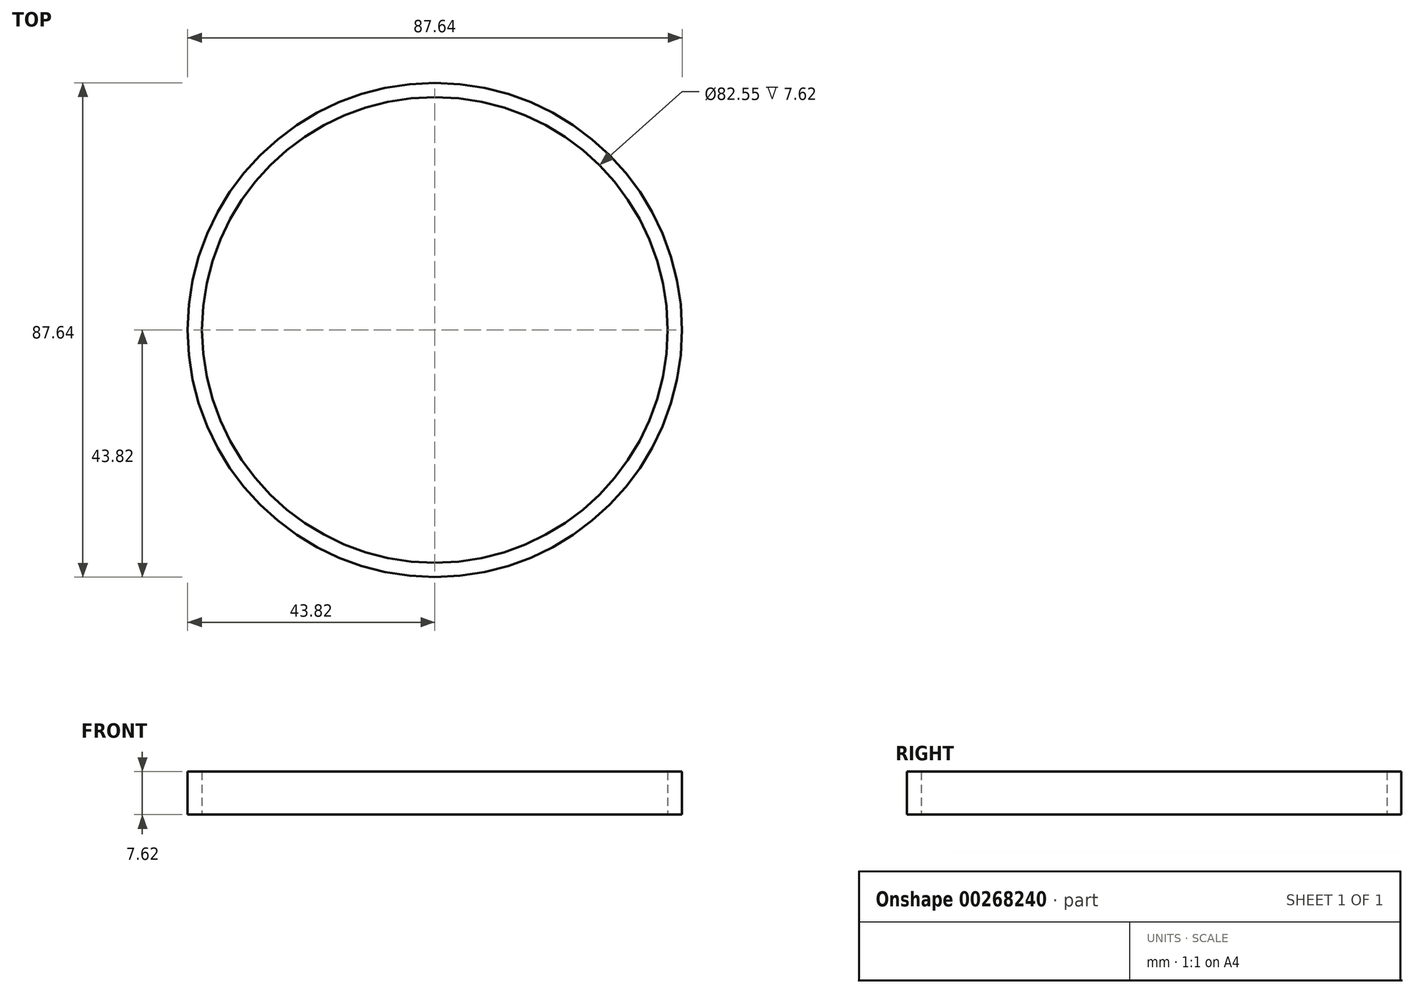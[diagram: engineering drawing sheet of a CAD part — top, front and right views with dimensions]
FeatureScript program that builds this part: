
annotation { "Feature Type Name" : "Feature", "Feature Type Description" : "" }
export const myFeature = defineFeature(function(context is Context, id is Id, definition is map)
    precondition{}
    {
        {
            var Q0;
            Q0=qCreatedBy(makeId("Top.planeOp"),FACE);
            var sketch = newSketch(context, id + "F0", { "sketchPlane" : qUnion([Q0])});
            skCircle(sketch, "E0", {"center": v(0, 0) * mm, "radius": 43.82 * mm});
            skCircle(sketch, "E1", {"center": v(0, 0) * mm, "radius": 41.28 * mm});
            skSolve(sketch);
        }
        {
            var Q0;
            Q0=makeQuery(id+"F0.imprint","IMPRINT",FACE,{"disambiguationData":[TD([[makeQuery(id+"F0.imprint","IMPRINT",EDGE,{"derivedFrom":sQuery(id+"F0.wireOp",EDGE,"E0")}),1.0]])]});
            extrude(context, id + "F1", {"entities" : qUnion([Q0]), "depth" : 7.62 * mm});
        }
    });
